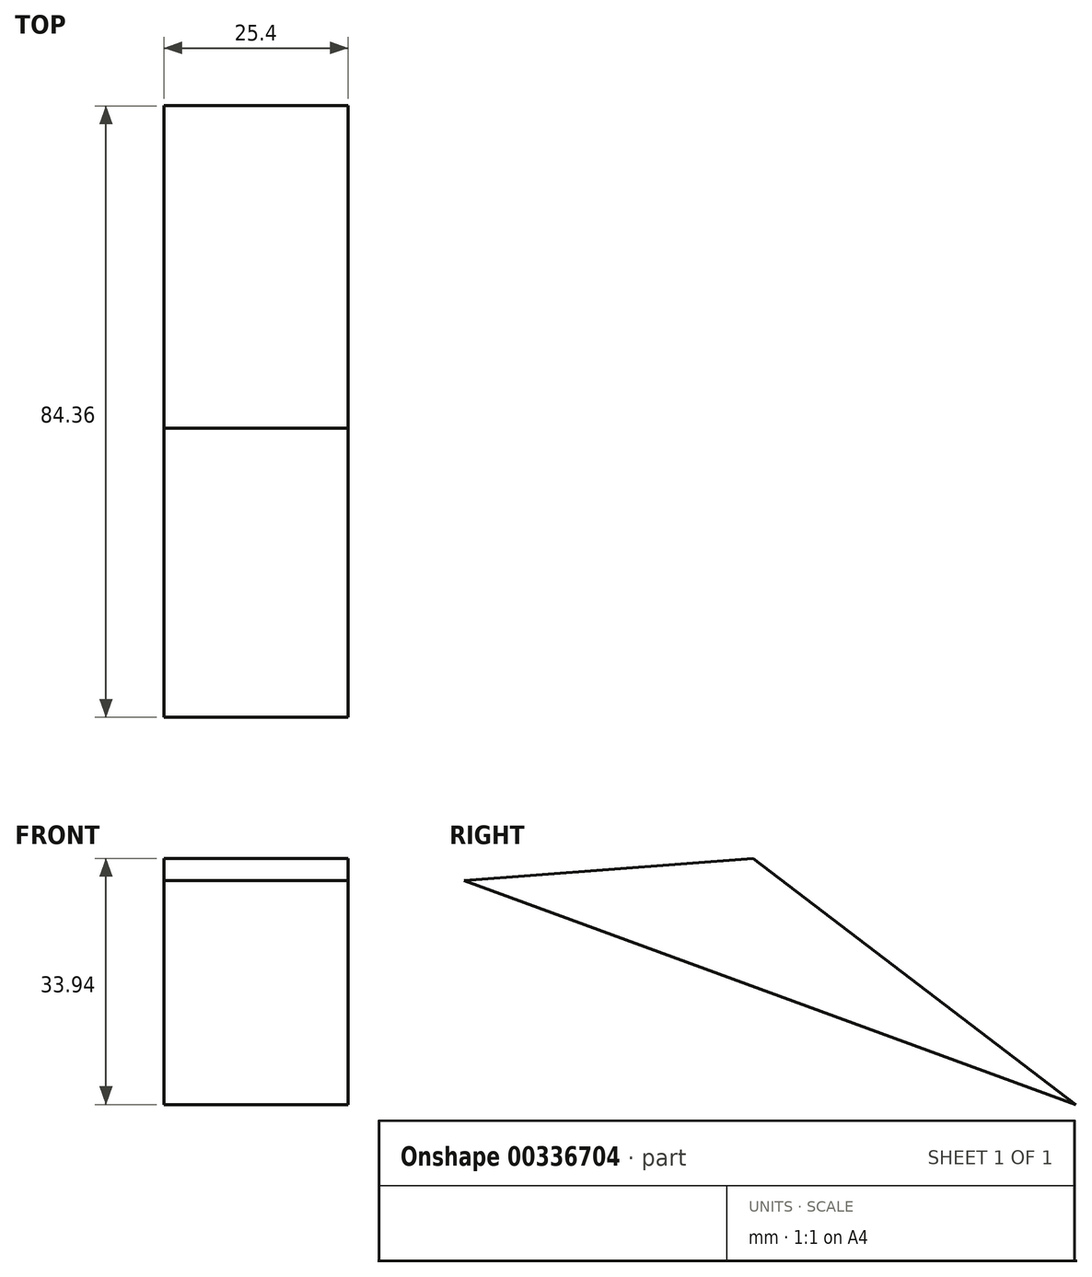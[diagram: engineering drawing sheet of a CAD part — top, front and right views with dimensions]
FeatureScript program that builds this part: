
annotation { "Feature Type Name" : "Feature", "Feature Type Description" : "" }
export const myFeature = defineFeature(function(context is Context, id is Id, definition is map)
    precondition{}
    {
        {
            var Q0;
            Q0=qCreatedBy(makeId("Right.planeOp"),FACE);
            var sketch = newSketch(context, id + "F0", { "sketchPlane" : qUnion([Q0])});
            skLineSegment(sketch, "E0", {"start": v(-39.88, 18.72) * mm, "end": v(0, 21.75) * mm});
            skLineSegment(sketch, "E1", {"start": v(0, 21.75) * mm, "end": v(44.48, -12.2) * mm});
            skLineSegment(sketch, "E2", {"start": v(44.48, -12.2) * mm, "end": v(-39.88, 18.72) * mm});
            skSolve(sketch);
        }
        {
            var Q0;
            Q0=makeQuery(id+"F0.imprint","IMPRINT",FACE,{"disambiguationData":[TD([[makeQuery(id+"F0.imprint","IMPRINT",EDGE,{"derivedFrom":sQuery(id+"F0.wireOp",EDGE,"E0")}),-1.0]])]});
            extrude(context, id + "F1", {"entities" : qUnion([Q0]), "depth" : 25.4 * mm});
        }
    });
